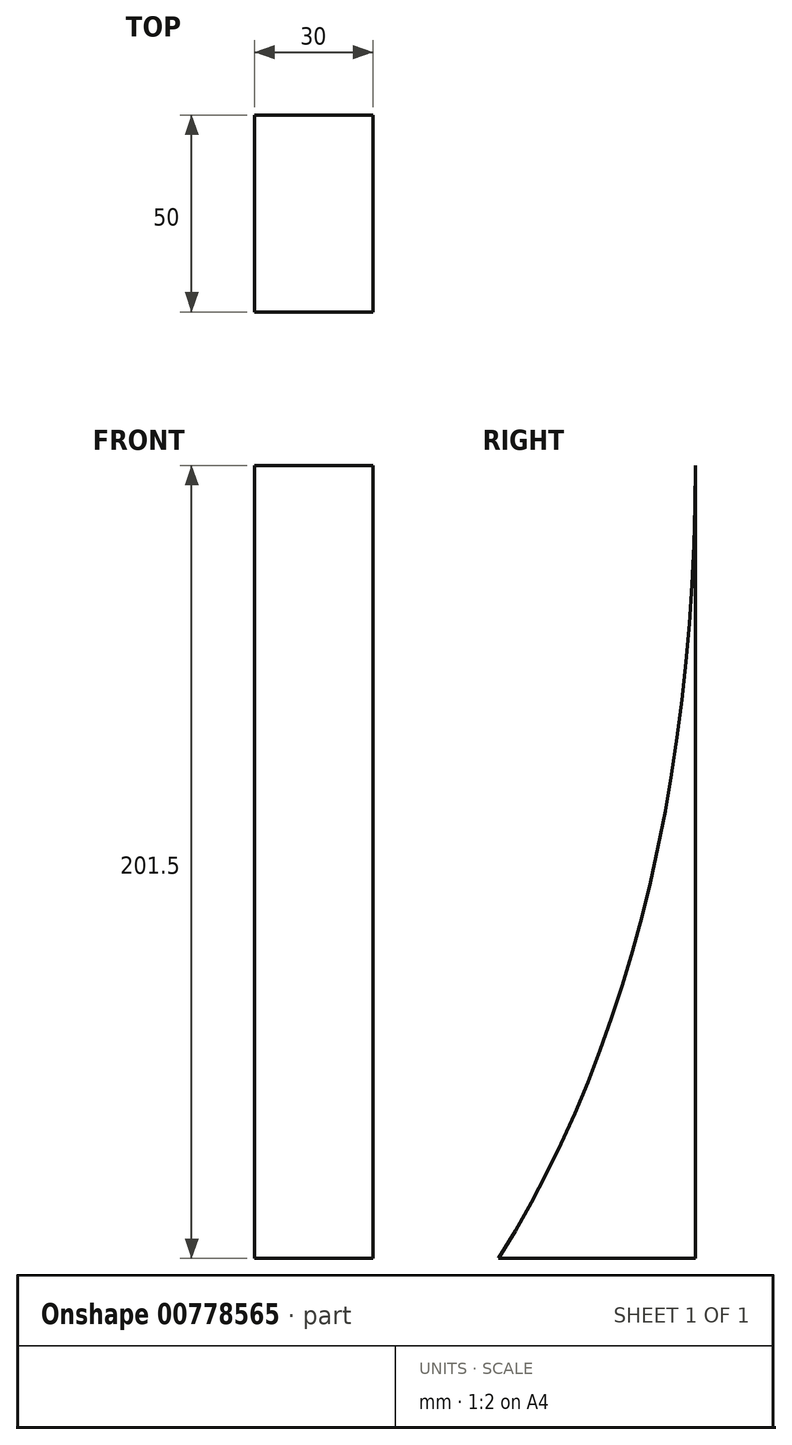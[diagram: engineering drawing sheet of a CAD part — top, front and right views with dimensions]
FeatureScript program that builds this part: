
annotation { "Feature Type Name" : "Feature", "Feature Type Description" : "" }
export const myFeature = defineFeature(function(context is Context, id is Id, definition is map)
    precondition{}
    {
        {
            var Q0;
            Q0=qCreatedBy(makeId("Right.planeOp"),FACE);
            var sketch = newSketch(context, id + "F0", { "sketchPlane" : qUnion([Q0])});
            skLineSegment(sketch, "E0.bottom", {"start": v(1350, -600) * mm, "end": v(-1350, -600) * mm});
            skLineSegment(sketch, "E0.top", {"start": v(1350, 600) * mm, "end": v(-1350, 600) * mm});
            skLineSegment(sketch, "E0.left", {"start": v(1350, -600) * mm, "end": v(1350, 600) * mm});
            skLineSegment(sketch, "E0.right", {"start": v(-1350, -600) * mm, "end": v(-1350, 600) * mm});
            skPoint(sketch, "E0.middle", {"position": v(0, 0) * mm});
            skFitSpline(sketch, "E1", {"points": [v(-1250, -600) * mm, v(-1305, 220) * mm, v(-750, 575) * mm, v(1055, 200) * mm, v(1300, -600) * mm], "startDerivative": vector(-1285.63, 2905.36) * mm, "endDerivative": vector(-1470.9, -2349.66) * mm});
            skLineSegment(sketch, "E2", {"start": v(1282.72, -570) * mm, "end": v(1229.8, -570) * mm});
            skFitSpline(sketch, "E3.0", {"points": [v(-1222.57, -587.86) * mm, v(-1229, -573.3) * mm, v(-1241.43, -542.74) * mm, v(-1264.19, -476.54) * mm, v(-1288.25, -385.83) * mm, v(-1308.86, -268.9) * mm, v(-1318.2, -168.56) * mm, v(-1320.44, -88.86) * mm, v(-1319.38, -29.94) * mm, v(-1315.47, 27.53) * mm, v(-1309.74, 73.73) * mm, v(-1303.64, 109.38) * mm, v(-1298.28, 135.39) * mm, v(-1292.15, 160.59) * mm, v(-1285.23, 184.91) * mm, v(-1277.52, 208.28) * mm, v(-1269.02, 230.63) * mm, v(-1259.7, 252.03) * mm, v(-1246.2, 279.3) * mm, v(-1227.24, 311.12) * mm, v(-1201.1, 345.96) * mm, v(-1171.41, 377.71) * mm, v(-1137.97, 406.6) * mm, v(-1100.56, 432.82) * mm, v(-1059, 456.49) * mm, v(-1013.11, 477.7) * mm, v(-962.78, 496.55) * mm, v(-907.9, 513.1) * mm, v(-858.31, 525.07) * mm, v(-816.3, 533.59) * mm, v(-783.6, 539.46) * mm, v(-749.7, 544.83) * mm, v(-714.62, 549.71) * mm, v(-678.4, 554.1) * mm, v(-628.7, 559.27) * mm, v(-564.07, 564.44) * mm, v(-483, 568.48) * mm, v(-398.93, 570.3) * mm, v(-312.34, 569.8) * mm, v(-194.18, 565.97) * mm, v(-42.62, 555.06) * mm, v(141.5, 531.6) * mm, v(323.98, 497.27) * mm, v(471.44, 459.15) * mm, v(584.7, 422.71) * mm, v(666.78, 392.37) * mm, v(745.52, 358.96) * mm, v(820.44, 322.43) * mm, v(891.05, 282.76) * mm, v(945.9, 247.05) * mm, v(987.16, 216.89) * mm, v(1011.8, 197.37) * mm, v(1030.8, 181.35) * mm, v(1049.33, 165.07) * mm, v(1071.6, 144.18) * mm, v(1096.95, 118.36) * mm, v(1128.9, 83.02) * mm, v(1165.37, 37.3) * mm, v(1203.65, -19.4) * mm, v(1236.46, -77.35) * mm, v(1263.83, -135.92) * mm, v(1285.8, -194.48) * mm, v(1302.4, -252.4) * mm, v(1313.68, -309.04) * mm, v(1319.7, -363.74) * mm, v(1320.57, -415.83) * mm, v(1316.37, -464.64) * mm, v(1307.27, -509.51) * mm, v(1293.48, -549.82) * mm, v(1281.34, -573.27) * mm, v(1274.57, -584.08) * mm]});
            skLineSegment(sketch, "E4", {"start": v(-1080.2, -570) * mm, "end": v(-1080.2, 444.2) * mm});
            skLineSegment(sketch, "E5", {"start": v(-1050.2, -570) * mm, "end": v(-1050.2, -450) * mm});
            skLineSegment(sketch, "E6", {"start": v(-1050.2, -570) * mm, "end": v(-450.2, -570) * mm});
            skLineSegment(sketch, "E7", {"start": v(-1080.2, -570) * mm, "end": v(-1230.2, -570) * mm});
            skLineSegment(sketch, "E8", {"start": v(-450.2, -570) * mm, "end": v(-450.2, -450) * mm});
            skLineSegment(sketch, "E9", {"start": v(-420.2, -570) * mm, "end": v(-420.2, 569.66) * mm});
            skFitSpline(sketch, "E10.trimOffspring", {"points": [v(-1222.57, -587.86) * mm, v(-1229, -573.3) * mm, v(-1241.43, -542.74) * mm, v(-1264.19, -476.54) * mm, v(-1288.25, -385.83) * mm, v(-1308.86, -268.9) * mm, v(-1318.2, -168.56) * mm, v(-1320.44, -88.86) * mm, v(-1319.38, -29.94) * mm, v(-1315.47, 27.53) * mm, v(-1309.74, 73.73) * mm, v(-1303.64, 109.38) * mm, v(-1298.28, 135.39) * mm, v(-1292.15, 160.59) * mm, v(-1285.23, 184.91) * mm, v(-1277.52, 208.28) * mm, v(-1269.02, 230.63) * mm, v(-1259.7, 252.03) * mm, v(-1246.2, 279.3) * mm, v(-1227.24, 311.12) * mm, v(-1201.1, 345.96) * mm, v(-1171.41, 377.71) * mm, v(-1137.97, 406.6) * mm, v(-1100.56, 432.82) * mm, v(-1059, 456.49) * mm, v(-1013.11, 477.7) * mm, v(-962.78, 496.55) * mm, v(-907.9, 513.1) * mm, v(-858.31, 525.07) * mm, v(-816.3, 533.59) * mm, v(-783.6, 539.46) * mm, v(-749.7, 544.83) * mm, v(-714.62, 549.71) * mm, v(-678.4, 554.1) * mm, v(-628.7, 559.27) * mm, v(-564.07, 564.44) * mm, v(-483, 568.48) * mm, v(-398.93, 570.3) * mm, v(-312.34, 569.8) * mm, v(-194.18, 565.97) * mm, v(-42.62, 555.06) * mm, v(141.5, 531.6) * mm, v(323.98, 497.27) * mm, v(471.44, 459.15) * mm, v(584.7, 422.71) * mm, v(666.78, 392.37) * mm, v(745.52, 358.96) * mm, v(820.44, 322.43) * mm, v(891.05, 282.76) * mm, v(945.9, 247.05) * mm, v(987.16, 216.89) * mm, v(1011.8, 197.37) * mm, v(1030.8, 181.35) * mm, v(1049.33, 165.07) * mm, v(1071.6, 144.18) * mm, v(1096.95, 118.36) * mm, v(1128.9, 83.02) * mm, v(1165.37, 37.3) * mm, v(1203.65, -19.4) * mm, v(1236.46, -77.35) * mm, v(1263.83, -135.92) * mm, v(1285.8, -194.48) * mm, v(1302.4, -252.4) * mm, v(1313.68, -309.04) * mm, v(1319.7, -363.74) * mm, v(1320.57, -415.83) * mm, v(1316.37, -464.64) * mm, v(1307.27, -509.51) * mm, v(1293.48, -549.82) * mm, v(1281.34, -573.27) * mm, v(1274.57, -584.08) * mm]});
            skFitSpline(sketch, "E11.trimOffspring", {"points": [v(-1222.57, -587.86) * mm, v(-1229, -573.3) * mm, v(-1241.43, -542.74) * mm, v(-1264.19, -476.54) * mm, v(-1288.25, -385.83) * mm, v(-1308.86, -268.9) * mm, v(-1318.2, -168.56) * mm, v(-1320.44, -88.86) * mm, v(-1319.38, -29.94) * mm, v(-1315.47, 27.53) * mm, v(-1309.74, 73.73) * mm, v(-1303.64, 109.38) * mm, v(-1298.28, 135.39) * mm, v(-1292.15, 160.59) * mm, v(-1285.23, 184.91) * mm, v(-1277.52, 208.28) * mm, v(-1269.02, 230.63) * mm, v(-1259.7, 252.03) * mm, v(-1246.2, 279.3) * mm, v(-1227.24, 311.12) * mm, v(-1201.1, 345.96) * mm, v(-1171.41, 377.71) * mm, v(-1137.97, 406.6) * mm, v(-1100.56, 432.82) * mm, v(-1059, 456.49) * mm, v(-1013.11, 477.7) * mm, v(-962.78, 496.55) * mm, v(-907.9, 513.1) * mm, v(-858.31, 525.07) * mm, v(-816.3, 533.59) * mm, v(-783.6, 539.46) * mm, v(-749.7, 544.83) * mm, v(-714.62, 549.71) * mm, v(-678.4, 554.1) * mm, v(-628.7, 559.27) * mm, v(-564.07, 564.44) * mm, v(-483, 568.48) * mm, v(-398.93, 570.3) * mm, v(-312.34, 569.8) * mm, v(-194.18, 565.97) * mm, v(-42.62, 555.06) * mm, v(141.5, 531.6) * mm, v(323.98, 497.27) * mm, v(471.44, 459.15) * mm, v(584.7, 422.71) * mm, v(666.78, 392.37) * mm, v(745.52, 358.96) * mm, v(820.44, 322.43) * mm, v(891.05, 282.76) * mm, v(945.9, 247.05) * mm, v(987.16, 216.89) * mm, v(1011.8, 197.37) * mm, v(1030.8, 181.35) * mm, v(1049.33, 165.07) * mm, v(1071.6, 144.18) * mm, v(1096.95, 118.36) * mm, v(1128.9, 83.02) * mm, v(1165.37, 37.3) * mm, v(1203.65, -19.4) * mm, v(1236.46, -77.35) * mm, v(1263.83, -135.92) * mm, v(1285.8, -194.48) * mm, v(1302.4, -252.4) * mm, v(1313.68, -309.04) * mm, v(1319.7, -363.74) * mm, v(1320.57, -415.83) * mm, v(1316.37, -464.64) * mm, v(1307.27, -509.51) * mm, v(1293.48, -549.82) * mm, v(1281.34, -573.27) * mm, v(1274.57, -584.08) * mm]});
            skLineSegment(sketch, "E12.trimOffspring", {"start": v(-450.2, -570) * mm, "end": v(-1050.2, -570) * mm});
            skLineSegment(sketch, "E13.trimOffspring", {"start": v(-1230.2, -570) * mm, "end": v(-1080.2, -570) * mm});
            skLineSegment(sketch, "E14.left", {"start": v(-120.2, -570) * mm, "end": v(-120.2, 560.2) * mm});
            skLineSegment(sketch, "E14.right", {"start": v(-90.2, -570) * mm, "end": v(-90.2, 557.77) * mm});
            skLineSegment(sketch, "E15.left", {"start": v(209.8, 518.19) * mm, "end": v(209.8, -570) * mm});
            skLineSegment(sketch, "E15.right", {"start": v(239.8, 512.6) * mm, "end": v(239.8, -570) * mm});
            skLineSegment(sketch, "E16.left", {"start": v(539.8, 437) * mm, "end": v(539.8, -570) * mm});
            skLineSegment(sketch, "E16.right", {"start": v(569.8, 427.13) * mm, "end": v(569.8, -570) * mm});
            skLineSegment(sketch, "E17.left", {"start": v(869.8, 294.34) * mm, "end": v(869.8, -570) * mm});
            skLineSegment(sketch, "E17.right", {"start": v(899.8, 276.4) * mm, "end": v(899.8, -570) * mm});
            skLineSegment(sketch, "E18.left", {"start": v(1199.8, -14.9) * mm, "end": v(1199.8, -570) * mm});
            skLineSegment(sketch, "E18.right", {"start": v(1229.8, -66.5) * mm, "end": v(1229.8, -570) * mm});
            skFitSpline(sketch, "E19.trimOffspring", {"points": [v(-1222.57, -587.86) * mm, v(-1229, -573.3) * mm, v(-1241.43, -542.74) * mm, v(-1264.19, -476.54) * mm, v(-1288.25, -385.83) * mm, v(-1308.86, -268.9) * mm, v(-1318.2, -168.56) * mm, v(-1320.44, -88.86) * mm, v(-1319.38, -29.94) * mm, v(-1315.47, 27.53) * mm, v(-1309.74, 73.73) * mm, v(-1303.64, 109.38) * mm, v(-1298.28, 135.39) * mm, v(-1292.15, 160.59) * mm, v(-1285.23, 184.91) * mm, v(-1277.52, 208.28) * mm, v(-1269.02, 230.63) * mm, v(-1259.7, 252.03) * mm, v(-1246.2, 279.3) * mm, v(-1227.24, 311.12) * mm, v(-1201.1, 345.96) * mm, v(-1171.41, 377.71) * mm, v(-1137.97, 406.6) * mm, v(-1100.56, 432.82) * mm, v(-1059, 456.49) * mm, v(-1013.11, 477.7) * mm, v(-962.78, 496.55) * mm, v(-907.9, 513.1) * mm, v(-858.31, 525.07) * mm, v(-816.3, 533.59) * mm, v(-783.6, 539.46) * mm, v(-749.7, 544.83) * mm, v(-714.62, 549.71) * mm, v(-678.4, 554.1) * mm, v(-628.7, 559.27) * mm, v(-564.07, 564.44) * mm, v(-483, 568.48) * mm, v(-398.93, 570.3) * mm, v(-312.34, 569.8) * mm, v(-194.18, 565.97) * mm, v(-42.62, 555.06) * mm, v(141.5, 531.6) * mm, v(323.98, 497.27) * mm, v(471.44, 459.15) * mm, v(584.7, 422.71) * mm, v(666.78, 392.37) * mm, v(745.52, 358.96) * mm, v(820.44, 322.43) * mm, v(891.05, 282.76) * mm, v(945.9, 247.05) * mm, v(987.16, 216.89) * mm, v(1011.8, 197.37) * mm, v(1030.8, 181.35) * mm, v(1049.33, 165.07) * mm, v(1071.6, 144.18) * mm, v(1096.95, 118.36) * mm, v(1128.9, 83.02) * mm, v(1165.37, 37.3) * mm, v(1203.65, -19.4) * mm, v(1236.46, -77.35) * mm, v(1263.83, -135.92) * mm, v(1285.8, -194.48) * mm, v(1302.4, -252.4) * mm, v(1313.68, -309.04) * mm, v(1319.7, -363.74) * mm, v(1320.57, -415.83) * mm, v(1316.37, -464.64) * mm, v(1307.27, -509.51) * mm, v(1293.48, -549.82) * mm, v(1281.34, -573.27) * mm, v(1274.57, -584.08) * mm]});
            skLineSegment(sketch, "E20.trimOffspring", {"start": v(1199.8, -570) * mm, "end": v(899.8, -570) * mm});
            skLineSegment(sketch, "E21.trimOffspring", {"start": v(869.8, -570) * mm, "end": v(569.8, -570) * mm});
            skLineSegment(sketch, "E22.trimOffspring", {"start": v(539.8, -570) * mm, "end": v(239.8, -570) * mm});
            skLineSegment(sketch, "E23.trimOffspring", {"start": v(209.8, -570) * mm, "end": v(-90.2, -570) * mm});
            skFitSpline(sketch, "E24.trimOffspring", {"points": [v(-1222.57, -587.86) * mm, v(-1229, -573.3) * mm, v(-1241.43, -542.74) * mm, v(-1264.19, -476.54) * mm, v(-1288.25, -385.83) * mm, v(-1308.86, -268.9) * mm, v(-1318.2, -168.56) * mm, v(-1320.44, -88.86) * mm, v(-1319.38, -29.94) * mm, v(-1315.47, 27.53) * mm, v(-1309.74, 73.73) * mm, v(-1303.64, 109.38) * mm, v(-1298.28, 135.39) * mm, v(-1292.15, 160.59) * mm, v(-1285.23, 184.91) * mm, v(-1277.52, 208.28) * mm, v(-1269.02, 230.63) * mm, v(-1259.7, 252.03) * mm, v(-1246.2, 279.3) * mm, v(-1227.24, 311.12) * mm, v(-1201.1, 345.96) * mm, v(-1171.41, 377.71) * mm, v(-1137.97, 406.6) * mm, v(-1100.56, 432.82) * mm, v(-1059, 456.49) * mm, v(-1013.11, 477.7) * mm, v(-962.78, 496.55) * mm, v(-907.9, 513.1) * mm, v(-858.31, 525.07) * mm, v(-816.3, 533.59) * mm, v(-783.6, 539.46) * mm, v(-749.7, 544.83) * mm, v(-714.62, 549.71) * mm, v(-678.4, 554.1) * mm, v(-628.7, 559.27) * mm, v(-564.07, 564.44) * mm, v(-483, 568.48) * mm, v(-398.93, 570.3) * mm, v(-312.34, 569.8) * mm, v(-194.18, 565.97) * mm, v(-42.62, 555.06) * mm, v(141.5, 531.6) * mm, v(323.98, 497.27) * mm, v(471.44, 459.15) * mm, v(584.7, 422.71) * mm, v(666.78, 392.37) * mm, v(745.52, 358.96) * mm, v(820.44, 322.43) * mm, v(891.05, 282.76) * mm, v(945.9, 247.05) * mm, v(987.16, 216.89) * mm, v(1011.8, 197.37) * mm, v(1030.8, 181.35) * mm, v(1049.33, 165.07) * mm, v(1071.6, 144.18) * mm, v(1096.95, 118.36) * mm, v(1128.9, 83.02) * mm, v(1165.37, 37.3) * mm, v(1203.65, -19.4) * mm, v(1236.46, -77.35) * mm, v(1263.83, -135.92) * mm, v(1285.8, -194.48) * mm, v(1302.4, -252.4) * mm, v(1313.68, -309.04) * mm, v(1319.7, -363.74) * mm, v(1320.57, -415.83) * mm, v(1316.37, -464.64) * mm, v(1307.27, -509.51) * mm, v(1293.48, -549.82) * mm, v(1281.34, -573.27) * mm, v(1274.57, -584.08) * mm]});
            skFitSpline(sketch, "E25.trimOffspring", {"points": [v(-1222.57, -587.86) * mm, v(-1229, -573.3) * mm, v(-1241.43, -542.74) * mm, v(-1264.19, -476.54) * mm, v(-1288.25, -385.83) * mm, v(-1308.86, -268.9) * mm, v(-1318.2, -168.56) * mm, v(-1320.44, -88.86) * mm, v(-1319.38, -29.94) * mm, v(-1315.47, 27.53) * mm, v(-1309.74, 73.73) * mm, v(-1303.64, 109.38) * mm, v(-1298.28, 135.39) * mm, v(-1292.15, 160.59) * mm, v(-1285.23, 184.91) * mm, v(-1277.52, 208.28) * mm, v(-1269.02, 230.63) * mm, v(-1259.7, 252.03) * mm, v(-1246.2, 279.3) * mm, v(-1227.24, 311.12) * mm, v(-1201.1, 345.96) * mm, v(-1171.41, 377.71) * mm, v(-1137.97, 406.6) * mm, v(-1100.56, 432.82) * mm, v(-1059, 456.49) * mm, v(-1013.11, 477.7) * mm, v(-962.78, 496.55) * mm, v(-907.9, 513.1) * mm, v(-858.31, 525.07) * mm, v(-816.3, 533.59) * mm, v(-783.6, 539.46) * mm, v(-749.7, 544.83) * mm, v(-714.62, 549.71) * mm, v(-678.4, 554.1) * mm, v(-628.7, 559.27) * mm, v(-564.07, 564.44) * mm, v(-483, 568.48) * mm, v(-398.93, 570.3) * mm, v(-312.34, 569.8) * mm, v(-194.18, 565.97) * mm, v(-42.62, 555.06) * mm, v(141.5, 531.6) * mm, v(323.98, 497.27) * mm, v(471.44, 459.15) * mm, v(584.7, 422.71) * mm, v(666.78, 392.37) * mm, v(745.52, 358.96) * mm, v(820.44, 322.43) * mm, v(891.05, 282.76) * mm, v(945.9, 247.05) * mm, v(987.16, 216.89) * mm, v(1011.8, 197.37) * mm, v(1030.8, 181.35) * mm, v(1049.33, 165.07) * mm, v(1071.6, 144.18) * mm, v(1096.95, 118.36) * mm, v(1128.9, 83.02) * mm, v(1165.37, 37.3) * mm, v(1203.65, -19.4) * mm, v(1236.46, -77.35) * mm, v(1263.83, -135.92) * mm, v(1285.8, -194.48) * mm, v(1302.4, -252.4) * mm, v(1313.68, -309.04) * mm, v(1319.7, -363.74) * mm, v(1320.57, -415.83) * mm, v(1316.37, -464.64) * mm, v(1307.27, -509.51) * mm, v(1293.48, -549.82) * mm, v(1281.34, -573.27) * mm, v(1274.57, -584.08) * mm]});
            skFitSpline(sketch, "E26.trimOffspring", {"points": [v(-1222.57, -587.86) * mm, v(-1229, -573.3) * mm, v(-1241.43, -542.74) * mm, v(-1264.19, -476.54) * mm, v(-1288.25, -385.83) * mm, v(-1308.86, -268.9) * mm, v(-1318.2, -168.56) * mm, v(-1320.44, -88.86) * mm, v(-1319.38, -29.94) * mm, v(-1315.47, 27.53) * mm, v(-1309.74, 73.73) * mm, v(-1303.64, 109.38) * mm, v(-1298.28, 135.39) * mm, v(-1292.15, 160.59) * mm, v(-1285.23, 184.91) * mm, v(-1277.52, 208.28) * mm, v(-1269.02, 230.63) * mm, v(-1259.7, 252.03) * mm, v(-1246.2, 279.3) * mm, v(-1227.24, 311.12) * mm, v(-1201.1, 345.96) * mm, v(-1171.41, 377.71) * mm, v(-1137.97, 406.6) * mm, v(-1100.56, 432.82) * mm, v(-1059, 456.49) * mm, v(-1013.11, 477.7) * mm, v(-962.78, 496.55) * mm, v(-907.9, 513.1) * mm, v(-858.31, 525.07) * mm, v(-816.3, 533.59) * mm, v(-783.6, 539.46) * mm, v(-749.7, 544.83) * mm, v(-714.62, 549.71) * mm, v(-678.4, 554.1) * mm, v(-628.7, 559.27) * mm, v(-564.07, 564.44) * mm, v(-483, 568.48) * mm, v(-398.93, 570.3) * mm, v(-312.34, 569.8) * mm, v(-194.18, 565.97) * mm, v(-42.62, 555.06) * mm, v(141.5, 531.6) * mm, v(323.98, 497.27) * mm, v(471.44, 459.15) * mm, v(584.7, 422.71) * mm, v(666.78, 392.37) * mm, v(745.52, 358.96) * mm, v(820.44, 322.43) * mm, v(891.05, 282.76) * mm, v(945.9, 247.05) * mm, v(987.16, 216.89) * mm, v(1011.8, 197.37) * mm, v(1030.8, 181.35) * mm, v(1049.33, 165.07) * mm, v(1071.6, 144.18) * mm, v(1096.95, 118.36) * mm, v(1128.9, 83.02) * mm, v(1165.37, 37.3) * mm, v(1203.65, -19.4) * mm, v(1236.46, -77.35) * mm, v(1263.83, -135.92) * mm, v(1285.8, -194.48) * mm, v(1302.4, -252.4) * mm, v(1313.68, -309.04) * mm, v(1319.7, -363.74) * mm, v(1320.57, -415.83) * mm, v(1316.37, -464.64) * mm, v(1307.27, -509.51) * mm, v(1293.48, -549.82) * mm, v(1281.34, -573.27) * mm, v(1274.57, -584.08) * mm]});
            skLineSegment(sketch, "E27.bottom", {"start": v(-1050.2, 210) * mm, "end": v(-450.2, 210) * mm});
            skLineSegment(sketch, "E27.top", {"start": v(-1050.2, 180) * mm, "end": v(-450.2, 180) * mm});
            skLineSegment(sketch, "E28.bottom", {"start": v(-450.2, -450) * mm, "end": v(-1050.2, -450) * mm});
            skLineSegment(sketch, "E28.top", {"start": v(-450.2, -420) * mm, "end": v(-1050.2, -420) * mm});
            skLineSegment(sketch, "E29.trimOffspring", {"start": v(-450.2, 210) * mm, "end": v(-450.2, 569.07) * mm});
            skLineSegment(sketch, "E30.trimOffspring", {"start": v(-1050.2, 210) * mm, "end": v(-1050.2, 460.14) * mm});
            skLineSegment(sketch, "E31.trimOffspring", {"start": v(-1050.2, -420) * mm, "end": v(-1050.2, 180) * mm});
            skLineSegment(sketch, "E32.trimOffspring", {"start": v(-120.2, -570) * mm, "end": v(-420.2, -570) * mm});
            skLineSegment(sketch, "E33.trimOffspring", {"start": v(-450.2, -420) * mm, "end": v(-450.2, 180) * mm});
            skSolve(sketch);
        }
        {
            var Q0;
            {var subQ0=sQuery(id+"F0.wireOp",EDGE,"E1");var subQ3=sQuery(id+"F0.wireOp",EDGE,"E0.bottom");var subQ4=makeQuery(id+"F0.imprint","INTERSECT",VERTEX,{"disambiguationData":[OD(0.0)],"derivedFrom":[subQ3,subQ0]});Q0=makeQuery(id+"F0.imprint","IMPRINT",FACE,{"disambiguationData":[TD([[makeQuery(id+"F0.imprint","IMPRINT",EDGE,{"disambiguationData":[TD([[subQ4,1.0]])],"derivedFrom":subQ3}),-1.0]])]});}
            extrude(context, id + "F1", {"entities" : qUnion([Q0]), "depth" : 30 * mm, "offsetDistance" : 25 * mm});
        }
        {
            var Q0;
            Q0=makeQuery(id+"F1.opExtrude","SWEPT_BODY",BODY,{"disambiguationData":[OSD([sQuery(id+"F0.wireOp",EDGE,"E0.bottom"),sQuery(id+"F0.wireOp",EDGE,"E1")])]});
            transform(context, id + "F2", {"entities" : qUnion([Q0]), "transformType" : TransformType.TRANSLATION_3D, "dx" : 0 * mm, "dy" : 0 * mm, "dz" : 0 * mm, "makeCopy" : true});
        }
        {
            var Q0;
            Q0=makeQuery(id+"F1.opExtrude","SWEPT_BODY",BODY,{"disambiguationData":[OSD([sQuery(id+"F0.wireOp",EDGE,"E0.bottom"),sQuery(id+"F0.wireOp",EDGE,"E1")])]});
            deleteBodies(context, id + "F3", {"entities" : qUnion([Q0])});
        }
        {
            var Q0;
            Q0=makeQuery(id+"F2.opPattern","COPY",BODY,{"derivedFrom":makeQuery(id+"F1.opExtrude","SWEPT_BODY",BODY,{"disambiguationData":[OSD([sQuery(id+"F0.wireOp",EDGE,"E0.bottom"),sQuery(id+"F0.wireOp",EDGE,"E1")])]}),"instanceName":"1"});
            transform(context, id + "F4", {"entities" : qUnion([Q0]), "transformType" : TransformType.TRANSLATION_3D, "dx" : 0 * mm, "dy" : 0 * mm, "dz" : 0 * mm, "makeCopy" : true});
        }
        {
            var Q0;
            Q0=makeQuery(id+"F4.opPattern","COPY",BODY,{"derivedFrom":makeQuery(id+"F2.opPattern","COPY",BODY,{"derivedFrom":makeQuery(id+"F1.opExtrude","SWEPT_BODY",BODY,{"disambiguationData":[OSD([sQuery(id+"F0.wireOp",EDGE,"E0.bottom"),sQuery(id+"F0.wireOp",EDGE,"E1"),sQuery(id+"F0.wireOp",EDGE,"E2"),sQuery(id+"F0.wireOp",EDGE,"E3.0"),sQuery(id+"F0.wireOp",EDGE,"E4"),sQuery(id+"F0.wireOp",EDGE,"E5"),sQuery(id+"F0.wireOp",EDGE,"E8"),sQuery(id+"F0.wireOp",EDGE,"E9"),sQuery(id+"F0.wireOp",EDGE,"E10.trimOffspring"),sQuery(id+"F0.wireOp",EDGE,"E11.trimOffspring"),sQuery(id+"F0.wireOp",EDGE,"E12.trimOffspring"),sQuery(id+"F0.wireOp",EDGE,"E7"),sQuery(id+"F0.wireOp",EDGE,"E14.left"),sQuery(id+"F0.wireOp",EDGE,"E14.right"),sQuery(id+"F0.wireOp",EDGE,"E15.left"),sQuery(id+"F0.wireOp",EDGE,"E15.right"),sQuery(id+"F0.wireOp",EDGE,"E16.left"),sQuery(id+"F0.wireOp",EDGE,"E16.right"),sQuery(id+"F0.wireOp",EDGE,"E17.left"),sQuery(id+"F0.wireOp",EDGE,"E17.right"),sQuery(id+"F0.wireOp",EDGE,"E18.left"),sQuery(id+"F0.wireOp",EDGE,"E18.right"),sQuery(id+"F0.wireOp",EDGE,"E19.trimOffspring"),sQuery(id+"F0.wireOp",EDGE,"E20.trimOffspring"),sQuery(id+"F0.wireOp",EDGE,"E21.trimOffspring"),sQuery(id+"F0.wireOp",EDGE,"E22.trimOffspring"),sQuery(id+"F0.wireOp",EDGE,"E23.trimOffspring"),sQuery(id+"F0.wireOp",EDGE,"E24.trimOffspring"),sQuery(id+"F0.wireOp",EDGE,"E25.trimOffspring"),sQuery(id+"F0.wireOp",EDGE,"E26.trimOffspring"),sQuery(id+"F0.wireOp",EDGE,"E27.bottom"),sQuery(id+"F0.wireOp",EDGE,"E27.top"),sQuery(id+"F0.wireOp",EDGE,"E28.bottom"),sQuery(id+"F0.wireOp",EDGE,"E28.top"),sQuery(id+"F0.wireOp",EDGE,"E29.trimOffspring"),sQuery(id+"F0.wireOp",EDGE,"E30.trimOffspring"),sQuery(id+"F0.wireOp",EDGE,"E31.trimOffspring"),sQuery(id+"F0.wireOp",EDGE,"E32.trimOffspring"),sQuery(id+"F0.wireOp",EDGE,"E33.trimOffspring")])]}),"instanceName":"1"}),"instanceName":"1"});
            deleteBodies(context, id + "F5", {"entities" : qUnion([Q0])});
        }
        {
            var Q0;
            Q0=makeQuery(id+"F2.opPattern","COPY",BODY,{"derivedFrom":makeQuery(id+"F1.opExtrude","SWEPT_BODY",BODY,{"disambiguationData":[OSD([sQuery(id+"F0.wireOp",EDGE,"E0.bottom"),sQuery(id+"F0.wireOp",EDGE,"E1"),sQuery(id+"F0.wireOp",EDGE,"E2"),sQuery(id+"F0.wireOp",EDGE,"E3.0"),sQuery(id+"F0.wireOp",EDGE,"E4"),sQuery(id+"F0.wireOp",EDGE,"E5"),sQuery(id+"F0.wireOp",EDGE,"E8"),sQuery(id+"F0.wireOp",EDGE,"E9"),sQuery(id+"F0.wireOp",EDGE,"E10.trimOffspring"),sQuery(id+"F0.wireOp",EDGE,"E11.trimOffspring"),sQuery(id+"F0.wireOp",EDGE,"E12.trimOffspring"),sQuery(id+"F0.wireOp",EDGE,"E7"),sQuery(id+"F0.wireOp",EDGE,"E14.left"),sQuery(id+"F0.wireOp",EDGE,"E14.right"),sQuery(id+"F0.wireOp",EDGE,"E15.left"),sQuery(id+"F0.wireOp",EDGE,"E15.right"),sQuery(id+"F0.wireOp",EDGE,"E16.left"),sQuery(id+"F0.wireOp",EDGE,"E16.right"),sQuery(id+"F0.wireOp",EDGE,"E17.left"),sQuery(id+"F0.wireOp",EDGE,"E17.right"),sQuery(id+"F0.wireOp",EDGE,"E18.left"),sQuery(id+"F0.wireOp",EDGE,"E18.right"),sQuery(id+"F0.wireOp",EDGE,"E19.trimOffspring"),sQuery(id+"F0.wireOp",EDGE,"E20.trimOffspring"),sQuery(id+"F0.wireOp",EDGE,"E21.trimOffspring"),sQuery(id+"F0.wireOp",EDGE,"E22.trimOffspring"),sQuery(id+"F0.wireOp",EDGE,"E23.trimOffspring"),sQuery(id+"F0.wireOp",EDGE,"E24.trimOffspring"),sQuery(id+"F0.wireOp",EDGE,"E25.trimOffspring"),sQuery(id+"F0.wireOp",EDGE,"E26.trimOffspring"),sQuery(id+"F0.wireOp",EDGE,"E27.bottom"),sQuery(id+"F0.wireOp",EDGE,"E27.top"),sQuery(id+"F0.wireOp",EDGE,"E28.bottom"),sQuery(id+"F0.wireOp",EDGE,"E28.top"),sQuery(id+"F0.wireOp",EDGE,"E29.trimOffspring"),sQuery(id+"F0.wireOp",EDGE,"E30.trimOffspring"),sQuery(id+"F0.wireOp",EDGE,"E31.trimOffspring"),sQuery(id+"F0.wireOp",EDGE,"E32.trimOffspring"),sQuery(id+"F0.wireOp",EDGE,"E33.trimOffspring")])]}),"instanceName":"1"});
            transform(context, id + "F6", {"entities" : qUnion([Q0]), "transformType" : TransformType.TRANSLATION_3D, "dx" : 0 * mm, "dy" : 0 * mm, "dz" : 0 * mm, "makeCopy" : true});
        }
    });
